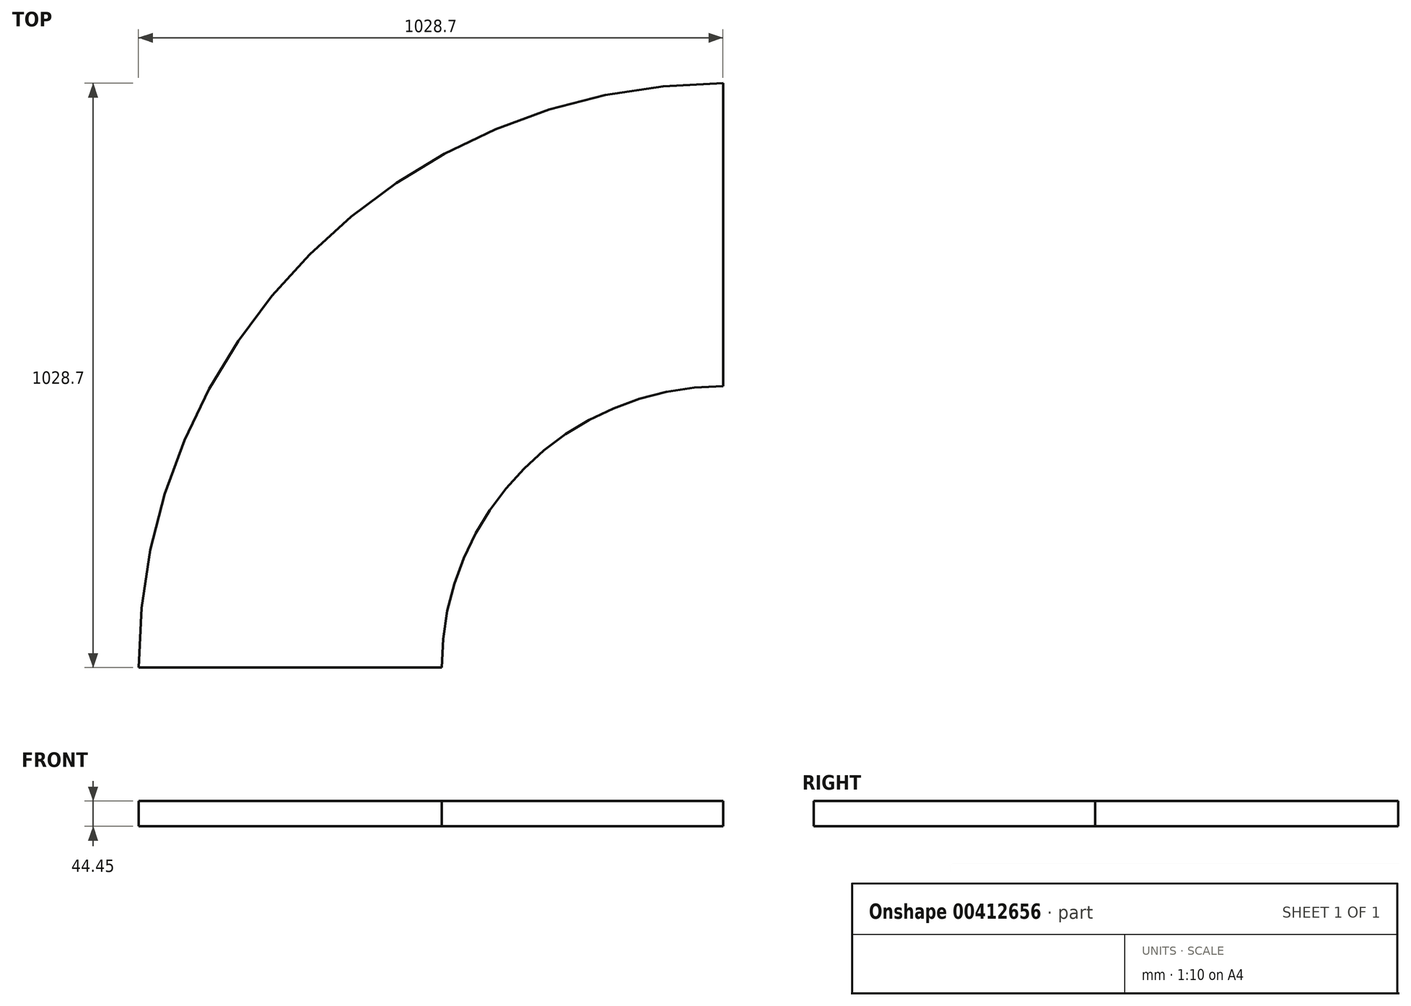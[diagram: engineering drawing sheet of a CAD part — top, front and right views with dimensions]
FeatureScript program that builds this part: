
annotation { "Feature Type Name" : "Feature", "Feature Type Description" : "" }
export const myFeature = defineFeature(function(context is Context, id is Id, definition is map)
    precondition{}
    {
        {
            var Q0;
            Q0=qCreatedBy(makeId("Top.planeOp"),FACE);
            var sketch = newSketch(context, id + "F0", { "sketchPlane" : qUnion([Q0])});
            skLineSegment(sketch, "E0", {"start": v(-19883.75, -1440.78) * mm, "end": v(-19387.66, -1440.78) * mm});
            skLineSegment(sketch, "E1", {"start": v(-22144.35, -1440.78) * mm, "end": v(-22334.85, -1440.78) * mm});
            skLineSegment(sketch, "E2", {"start": v(-24900.25, -1440.78) * mm, "end": v(-24900.25, -1186.8) * mm});
            skLineSegment(sketch, "E3", {"start": v(-24900.25, -1440.78) * mm, "end": v(-24595.45, -1440.78) * mm});
            skLineSegment(sketch, "E4", {"start": v(-19223.35, 939.75) * mm, "end": v(-19445.84, 939.75) * mm});
            skArc(sketch, "E5", {"start": v(-23624.14, 124.14) * mm, "mid": v(-23629.69, 120.5) * mm, "end": v(-23635.25, 116.9) * mm});
            skArc(sketch, "E6", {"start": v(-22416.05, -766.1) * mm, "mid": v(-22355.33, -972.57) * mm, "end": v(-22334.85, -1186.8) * mm});
            skLineSegment(sketch, "E7", {"start": v(-22334.85, -1186.8) * mm, "end": v(-22334.85, -1440.78) * mm});
            skLineSegment(sketch, "E8", {"start": v(-22334.85, -1440.78) * mm, "end": v(-22144.35, -1440.78) * mm});
            skLineSegment(sketch, "E9", {"start": v(-22144.35, -1440.78) * mm, "end": v(-22144.35, -1186.8) * mm});
            skArc(sketch, "E10", {"start": v(-22144.35, -1186.8) * mm, "mid": v(-21879.66, -459.96) * mm, "end": v(-21209.55, -73.54) * mm});
            skArc(sketch, "E11", {"start": v(-21209.55, -73.54) * mm, "mid": v(-20505.5, -177.37) * mm, "end": v(-20003.05, -681.36) * mm});
            skArc(sketch, "E12", {"start": v(-18796.55, -356.38) * mm, "mid": v(-18777.6, -346.4) * mm, "end": v(-18758.45, -336.8) * mm});
            skArc(sketch, "E13", {"start": v(-18758.45, -336.8) * mm, "mid": v(-18387.2, -228.46) * mm, "end": v(-18001.15, -251.63) * mm});
            skLineSegment(sketch, "E14", {"start": v(-18001.15, -251.63) * mm, "end": v(-18051.16, -107.3) * mm});
            skLineSegment(sketch, "E15", {"start": v(-18051.16, -107.3) * mm, "end": v(-18758.45, -107.3) * mm});
            skLineSegment(sketch, "E16", {"start": v(-18758.45, -107.3) * mm, "end": v(-19191.6, -107.3) * mm});
            skLineSegment(sketch, "E17", {"start": v(-19915.5, 31.7) * mm, "end": v(-19191.6, 31.7) * mm});
            skLineSegment(sketch, "E18", {"start": v(-19191.6, 31.7) * mm, "end": v(-19191.6, -692.2) * mm});
            skLineSegment(sketch, "E19", {"start": v(-19191.6, -692.2) * mm, "end": v(-19915.5, -692.2) * mm});
            skLineSegment(sketch, "E20", {"start": v(-19915.5, -692.2) * mm, "end": v(-19915.5, 31.7) * mm});
            skLineSegment(sketch, "E21", {"start": v(-7944.98, -1186.24) * mm, "end": v(-6763.86, -1186.24) * mm});
            skLineSegment(sketch, "E22", {"start": v(-6763.86, -1186.24) * mm, "end": v(-6763.86, 896.56) * mm});
            skLineSegment(sketch, "E23", {"start": v(-6763.86, 896.56) * mm, "end": v(-7944.98, 896.56) * mm});
            skLineSegment(sketch, "E24", {"start": v(-7944.98, 896.56) * mm, "end": v(-7944.98, 895.72) * mm});
            skLineSegment(sketch, "E25", {"start": v(-7944.98, 895.72) * mm, "end": v(-7944.98, 896.56) * mm});
            skArc(sketch, "E26", {"start": v(-7944.98, 895.72) * mm, "mid": v(-6945.35, -144.84) * mm, "end": v(-7944.98, -1185.4) * mm});
            skLineSegment(sketch, "E27", {"start": v(-7944.98, -1185.4) * mm, "end": v(-7944.98, -1186.24) * mm});
            skLineSegment(sketch, "E28", {"start": v(-7944.98, -1186.24) * mm, "end": v(-7944.98, -1185.4) * mm});
            skArc(sketch, "E29", {"start": v(-26035.55, -56.51) * mm, "mid": v(-26054.6, -56.76) * mm, "end": v(-26073.65, -57.33) * mm});
            skArc(sketch, "E30", {"start": v(-26073.65, -57.33) * mm, "mid": v(-26668.13, -253.5) * mm, "end": v(-27067.03, -735.95) * mm});
            skArc(sketch, "E31", {"start": v(-27067.03, -735.95) * mm, "mid": v(-27162.82, 105.98) * mm, "end": v(-27011.71, 939.75) * mm});
            skArc(sketch, "E32", {"start": v(-27011.71, 939.75) * mm, "mid": v(-26739.24, 262.5) * mm, "end": v(-26073.65, -37.34) * mm});
            skArc(sketch, "E33", {"start": v(-26073.65, -37.34) * mm, "mid": v(-26054.6, -37.93) * mm, "end": v(-26035.55, -38.15) * mm});
            skLineSegment(sketch, "E34", {"start": v(9209.44, 317.07) * mm, "end": v(9047.31, 575.14) * mm});
            skLineSegment(sketch, "E35", {"start": v(9047.31, 575.14) * mm, "end": v(9209.44, 317.07) * mm});
            skLineSegment(sketch, "E36", {"start": v(9209.44, 317.07) * mm, "end": v(9274.99, 358.25) * mm});
            skLineSegment(sketch, "E37", {"start": v(9274.99, 358.25) * mm, "end": v(9274.99, 1214.98) * mm});
            skLineSegment(sketch, "E38", {"start": v(9274.99, 1214.98) * mm, "end": v(7335.84, 1214.98) * mm});
            skLineSegment(sketch, "E39", {"start": v(7335.84, 1214.98) * mm, "end": v(7211.7, 630.91) * mm});
            skLineSegment(sketch, "E40", {"start": v(7211.7, 630.91) * mm, "end": v(6857.64, 706.17) * mm});
            skLineSegment(sketch, "E41", {"start": v(6857.64, 706.17) * mm, "end": v(6563.71, -676.62) * mm});
            skLineSegment(sketch, "E42", {"start": v(6563.71, -676.62) * mm, "end": v(7358.75, -845.61) * mm});
            skLineSegment(sketch, "E43", {"start": v(7358.75, -845.61) * mm, "end": v(7424.3, -804.44) * mm});
            skLineSegment(sketch, "E44", {"start": v(7424.3, -804.44) * mm, "end": v(7262.17, -546.36) * mm});
            skArc(sketch, "E45", {"start": v(7262.17, -546.36) * mm, "mid": v(7100.9, 38.05) * mm, "end": v(7288.24, 614.64) * mm});
            skArc(sketch, "E46", {"start": v(7288.24, 614.64) * mm, "mid": v(8178.4, 1068.22) * mm, "end": v(9047.31, 575.14) * mm});
            skArc(sketch, "E47", {"start": v(-26035.55, -56.51) * mm, "mid": v(-25233.08, -385.8) * mm, "end": v(-24900.25, -1186.8) * mm});
            skLineSegment(sketch, "E48", {"start": v(-24900.25, -1186.8) * mm, "end": v(-24900.25, -1440.78) * mm});
            skLineSegment(sketch, "E49", {"start": v(-24900.25, -1440.78) * mm, "end": v(-24829.05, -1440.78) * mm});
            skArc(sketch, "E50", {"start": v(-21209.55, 357.7) * mm, "mid": v(-21296.65, 498.93) * mm, "end": v(-21358.61, 652.85) * mm});
            skArc(sketch, "E51", {"start": v(-21358.61, 652.85) * mm, "mid": v(-21762.75, 118.4) * mm, "end": v(-22416.05, -30.44) * mm});
            skArc(sketch, "E52", {"start": v(-22416.05, -30.44) * mm, "mid": v(-22923.26, 191.64) * mm, "end": v(-23228.56, 653.55) * mm});
            skArc(sketch, "E53", {"start": v(-23228.56, 653.55) * mm, "mid": v(-23379.7, 355.18) * mm, "end": v(-23622.55, 125.19) * mm});
            skArc(sketch, "E54", {"start": v(-23635.25, -69.38) * mm, "mid": v(-23628.9, -68.43) * mm, "end": v(-23622.55, -67.52) * mm});
            skArc(sketch, "E55", {"start": v(-23622.55, 125.19) * mm, "mid": v(-24242.78, -34.94) * mm, "end": v(-24829.05, 223.15) * mm});
            skLineSegment(sketch, "E56", {"start": v(-30175.2, -6534.7) * mm, "end": v(-30175.2, 5657.3) * mm});
            skLineSegment(sketch, "E57", {"start": v(-30175.2, 5657.3) * mm, "end": v(30710.16, 5657.3) * mm});
            skLineSegment(sketch, "E58", {"start": v(30710.16, 5657.3) * mm, "end": v(30710.16, -6534.7) * mm});
            skLineSegment(sketch, "E59", {"start": v(30710.16, -6534.7) * mm, "end": v(-30175.2, -6534.7) * mm});
            skLineSegment(sketch, "E60", {"start": v(-30175.2, 5657.3) * mm, "end": v(-14935.2, 5657.3) * mm});
            skLineSegment(sketch, "E61", {"start": v(-14935.2, 5657.3) * mm, "end": v(-14935.2, -6534.7) * mm});
            skCircle(sketch, "E62", {"center": v(8154.74, 14.39) * mm, "radius": 533.4 * mm});
            skArc(sketch, "E63", {"start": v(8531.12, 250.85) * mm, "mid": v(7918.28, 390.77) * mm, "end": v(7778.35, -222.07) * mm});
            skArc(sketch, "E64", {"start": v(9047.31, 575.14) * mm, "mid": v(7593.99, 906.96) * mm, "end": v(7262.17, -546.36) * mm});
            skLineSegment(sketch, "E65", {"start": v(7531.84, -736.88) * mm, "end": v(7940.48, -480.15) * mm});
            skLineSegment(sketch, "E66", {"start": v(7531.84, -736.88) * mm, "end": v(7424.3, -804.44) * mm});
            skLineSegment(sketch, "E67", {"start": v(7778.35, -222.07) * mm, "end": v(7940.48, -480.15) * mm});
            skLineSegment(sketch, "E68", {"start": v(7262.17, -546.36) * mm, "end": v(7424.3, -804.44) * mm});
            skLineSegment(sketch, "E69", {"start": v(9101.9, 249.5) * mm, "end": v(8693.26, -7.22) * mm});
            skLineSegment(sketch, "E70", {"start": v(9101.9, 249.5) * mm, "end": v(9209.44, 317.07) * mm});
            skLineSegment(sketch, "E71", {"start": v(8531.12, 250.85) * mm, "end": v(8693.26, -7.22) * mm});
            skLineSegment(sketch, "E72", {"start": v(8939.77, 507.58) * mm, "end": v(9101.9, 249.5) * mm});
            skLineSegment(sketch, "E73", {"start": v(7369.7, -478.8) * mm, "end": v(7531.84, -736.88) * mm});
            skArc(sketch, "E74", {"start": v(8939.77, 507.58) * mm, "mid": v(7661.55, 799.42) * mm, "end": v(7369.7, -478.8) * mm});
            skCircle(sketch, "E75", {"center": v(-23465.15, -1186.8) * mm, "radius": 609.6 * mm});
            skLineSegment(sketch, "E76", {"start": v(-24493.85, -1491.58) * mm, "end": v(-23985.85, -1491.58) * mm});
            skLineSegment(sketch, "E77", {"start": v(-22944.45, -1491.58) * mm, "end": v(-22436.45, -1491.58) * mm});
            skLineSegment(sketch, "E78", {"start": v(-24493.85, -1491.58) * mm, "end": v(-24595.45, -1491.58) * mm});
            skLineSegment(sketch, "E79", {"start": v(-22334.85, -1491.58) * mm, "end": v(-22436.45, -1491.58) * mm});
            skLineSegment(sketch, "E80", {"start": v(-22944.45, -1491.58) * mm, "end": v(-22944.45, -1186.8) * mm});
            skArc(sketch, "E81", {"start": v(-22944.45, -1186.8) * mm, "mid": v(-23465.15, -666.1) * mm, "end": v(-23985.85, -1186.8) * mm});
            skLineSegment(sketch, "E82", {"start": v(-23985.85, -1186.8) * mm, "end": v(-23985.85, -1491.58) * mm});
            skLineSegment(sketch, "E83", {"start": v(-22461.85, -1491.58) * mm, "end": v(-22461.85, -1186.8) * mm});
            skArc(sketch, "E84", {"start": v(-22461.85, -1186.8) * mm, "mid": v(-23465.15, -183.5) * mm, "end": v(-24468.45, -1186.8) * mm});
            skLineSegment(sketch, "E85", {"start": v(-24468.45, -1186.8) * mm, "end": v(-24468.45, -1491.58) * mm});
            skLineSegment(sketch, "E86", {"start": v(-24595.45, -1491.58) * mm, "end": v(-24595.45, -1186.8) * mm});
            skArc(sketch, "E87", {"start": v(-24595.45, -1186.8) * mm, "mid": v(-23465.15, -56.5) * mm, "end": v(-22334.85, -1186.8) * mm});
            skLineSegment(sketch, "E88", {"start": v(-22334.85, -1186.8) * mm, "end": v(-22334.85, -1491.58) * mm});
            skCircle(sketch, "E89", {"center": v(-21014.05, -1186.8) * mm, "radius": 609.6 * mm});
            skLineSegment(sketch, "E90", {"start": v(-22042.75, -1491.58) * mm, "end": v(-21534.75, -1491.58) * mm});
            skLineSegment(sketch, "E91", {"start": v(-20493.35, -1491.58) * mm, "end": v(-19985.35, -1491.58) * mm});
            skLineSegment(sketch, "E92", {"start": v(-22042.75, -1491.58) * mm, "end": v(-22144.35, -1491.58) * mm});
            skLineSegment(sketch, "E93", {"start": v(-19883.75, -1491.58) * mm, "end": v(-19985.35, -1491.58) * mm});
            skLineSegment(sketch, "E94", {"start": v(-20493.35, -1491.58) * mm, "end": v(-20493.35, -1186.8) * mm});
            skArc(sketch, "E95", {"start": v(-20493.35, -1186.8) * mm, "mid": v(-21014.05, -666.1) * mm, "end": v(-21534.75, -1186.8) * mm});
            skLineSegment(sketch, "E96", {"start": v(-21534.75, -1186.8) * mm, "end": v(-21534.75, -1491.58) * mm});
            skLineSegment(sketch, "E97", {"start": v(-22144.35, -1491.58) * mm, "end": v(-22144.35, -1186.8) * mm});
            skArc(sketch, "E98", {"start": v(-22144.35, -1186.8) * mm, "mid": v(-21014.05, -56.5) * mm, "end": v(-19883.75, -1186.8) * mm});
            skLineSegment(sketch, "E99", {"start": v(-19883.75, -1186.8) * mm, "end": v(-19883.75, -1491.58) * mm});
            skCircle(sketch, "E100", {"center": v(-18260.88, -1351.68) * mm, "radius": 609.6 * mm});
            skArc(sketch, "E101", {"start": v(-17495.42, -2183.33) * mm, "mid": v(-17871.86, -290.44) * mm, "end": v(-19382.5, -1491.58) * mm});
            skArc(sketch, "E102", {"start": v(-17908.25, -1734.8) * mm, "mid": v(-18051.7, -874.85) * mm, "end": v(-18781.58, -1351.68) * mm});
            skLineSegment(sketch, "E103", {"start": v(-17495.42, -2183.33) * mm, "end": v(-17908.25, -1734.8) * mm});
            skLineSegment(sketch, "E104", {"start": v(-19883.75, -1491.58) * mm, "end": v(-19883.75, -1440.78) * mm});
            skCircle(sketch, "E105", {"center": v(-26030.55, -1186.8) * mm, "radius": 609.6 * mm});
            skLineSegment(sketch, "E106", {"start": v(-25001.85, -1491.58) * mm, "end": v(-25509.85, -1491.58) * mm});
            skLineSegment(sketch, "E107", {"start": v(-24900.25, -1491.58) * mm, "end": v(-24900.25, -1186.8) * mm});
            skArc(sketch, "E108", {"start": v(-24900.25, -1186.8) * mm, "mid": v(-26560.4, -188.39) * mm, "end": v(-26664.1, -2122.86) * mm});
            skArc(sketch, "E109", {"start": v(-25027.25, -1186.8) * mm, "mid": v(-26500.86, -300.57) * mm, "end": v(-26592.9, -2017.68) * mm});
            skLineSegment(sketch, "E110", {"start": v(-25001.85, -1491.58) * mm, "end": v(-24900.25, -1491.58) * mm});
            skArc(sketch, "E111", {"start": v(-26322.4, -1618.02) * mm, "mid": v(-26274.63, -726.86) * mm, "end": v(-25509.85, -1186.8) * mm});
            skLineSegment(sketch, "E112", {"start": v(-25509.85, -1186.8) * mm, "end": v(-25509.85, -1491.58) * mm});
            skLineSegment(sketch, "E113", {"start": v(-20010.75, -1491.58) * mm, "end": v(-20010.75, -1186.8) * mm});
            skArc(sketch, "E114", {"start": v(-20010.75, -1186.8) * mm, "mid": v(-21014.05, -183.5) * mm, "end": v(-22017.35, -1186.8) * mm});
            skLineSegment(sketch, "E115", {"start": v(-22017.35, -1186.8) * mm, "end": v(-22017.35, -1491.58) * mm});
            skArc(sketch, "E116", {"start": v(-17581.43, -2089.9) * mm, "mid": v(-17923.02, -406.98) * mm, "end": v(-19254.38, -1491.58) * mm});
            skLineSegment(sketch, "E117", {"start": v(-24976.45, -1186.8) * mm, "end": v(-24976.45, -1491.58) * mm});
            skLineSegment(sketch, "E118", {"start": v(-25027.25, -1186.8) * mm, "end": v(-25027.25, -1491.58) * mm});
            skLineSegment(sketch, "E119", {"start": v(-26664.1, -2122.86) * mm, "end": v(-26322.4, -1618.02) * mm});
            skLineSegment(sketch, "E120", {"start": v(-19382.5, -1491.58) * mm, "end": v(-18781.58, -1491.58) * mm});
            skLineSegment(sketch, "E121", {"start": v(-18781.58, -1351.68) * mm, "end": v(-18781.58, -1491.58) * mm});
            skArc(sketch, "E122", {"start": v(-23622.55, -67.52) * mm, "mid": v(-22898.77, -208.64) * mm, "end": v(-22416.05, -766.1) * mm});
            skArc(sketch, "E123", {"start": v(-20003.05, -681.36) * mm, "mid": v(-19990, -708.37) * mm, "end": v(-19977.65, -735.73) * mm});
            skArc(sketch, "E124", {"start": v(-19977.65, -735.73) * mm, "mid": v(-19907.47, -956.43) * mm, "end": v(-19883.75, -1186.8) * mm});
            skLineSegment(sketch, "E125", {"start": v(-19883.75, -1186.8) * mm, "end": v(-19883.75, -1440.78) * mm});
            skArc(sketch, "E126", {"start": v(-19387.66, -1440.78) * mm, "mid": v(-19253.31, -810.7) * mm, "end": v(-18796.55, -356.38) * mm});
            skArc(sketch, "E127", {"start": v(-20003.05, 56.97) * mm, "mid": v(-20660.26, -9.12) * mm, "end": v(-21209.55, 357.7) * mm});
            skLineSegment(sketch, "E128", {"start": v(-24519.25, -120.7) * mm, "end": v(-24519.25, -577.9) * mm});
            skLineSegment(sketch, "E129", {"start": v(-24519.25, -577.9) * mm, "end": v(-24976.45, -577.9) * mm});
            skLineSegment(sketch, "E130", {"start": v(-24976.45, -577.9) * mm, "end": v(-24976.45, -120.7) * mm});
            skLineSegment(sketch, "E131", {"start": v(-24976.45, -120.7) * mm, "end": v(-24519.25, -120.7) * mm});
            skArc(sketch, "E132", {"start": v(-24829.05, 223.15) * mm, "mid": v(-24992.32, 420.54) * mm, "end": v(-25098.73, 653.55) * mm});
            skArc(sketch, "E133", {"start": v(-25098.73, 653.55) * mm, "mid": v(-25452.96, 153.05) * mm, "end": v(-26035.55, -38.15) * mm});
            skLineSegment(sketch, "E134", {"start": v(-24829.05, -1440.78) * mm, "end": v(-24595.45, -1440.78) * mm});
            skLineSegment(sketch, "E135", {"start": v(-24595.45, -1440.78) * mm, "end": v(-24595.45, -1186.8) * mm});
            skArc(sketch, "E136", {"start": v(-24595.45, -1186.8) * mm, "mid": v(-24322.42, -450.15) * mm, "end": v(-23635.25, -69.38) * mm});
            skCircle(sketch, "E137", {"center": v(-24163.65, 939.75) * mm, "radius": 457.2 * mm});
            skArc(sketch, "E138", {"start": v(-24902.75, 518.14) * mm, "mid": v(-24167.3, 88.86) * mm, "end": v(-23428.19, 511.81) * mm});
            skArc(sketch, "E139", {"start": v(-25098.73, 653.55) * mm, "mid": v(-24163.65, -38.15) * mm, "end": v(-23228.56, 653.55) * mm});
            skArc(sketch, "E140", {"start": v(-24564.03, 911.62) * mm, "mid": v(-25102.8, 1111.21) * mm, "end": v(-25637.83, 901.84) * mm});
            skArc(sketch, "E141", {"start": v(-24517.82, 838.72) * mm, "mid": v(-24535.66, 878.5) * mm, "end": v(-24564.03, 911.62) * mm});
            skArc(sketch, "E142", {"start": v(-24517.82, 838.72) * mm, "mid": v(-24166.57, 571.46) * mm, "end": v(-23811.12, 833.1) * mm});
            skArc(sketch, "E143", {"start": v(-23767.67, 901.84) * mm, "mid": v(-23794.06, 870.42) * mm, "end": v(-23811.12, 833.1) * mm});
            skLineSegment(sketch, "E144", {"start": v(-26531.71, 939.75) * mm, "end": v(-27011.71, 939.75) * mm});
            skCircle(sketch, "E145", {"center": v(-26033.81, 939.75) * mm, "radius": 457.2 * mm});
            skArc(sketch, "E146", {"start": v(-26884.71, 939.75) * mm, "mid": v(-26251.9, 117.27) * mm, "end": v(-25294.7, 518.14) * mm});
            skArc(sketch, "E147", {"start": v(-27011.71, 939.75) * mm, "mid": v(-26178.5, -27.39) * mm, "end": v(-25098.73, 653.55) * mm});
            skArc(sketch, "E148", {"start": v(-26385.98, 831.95) * mm, "mid": v(-26033.21, 571.45) * mm, "end": v(-25681.29, 833.1) * mm});
            skArc(sketch, "E149", {"start": v(-26385.98, 831.95) * mm, "mid": v(-26441.08, 909.87) * mm, "end": v(-26531.71, 939.75) * mm});
            skArc(sketch, "E150", {"start": v(-25637.83, 901.84) * mm, "mid": v(-25664.23, 870.42) * mm, "end": v(-25681.29, 833.1) * mm});
            skArc(sketch, "E151", {"start": v(-25098.73, 653.55) * mm, "mid": v(-25230.44, 583.03) * mm, "end": v(-25325.7, 467.93) * mm});
            skLineSegment(sketch, "E152", {"start": v(-25098.73, 1110.75) * mm, "end": v(-25098.73, 653.55) * mm});
            skArc(sketch, "E153", {"start": v(-24871.76, 467.93) * mm, "mid": v(-24966.62, 583.51) * mm, "end": v(-25098.73, 653.55) * mm});
            skCircle(sketch, "E154", {"center": v(-22293.48, 939.75) * mm, "radius": 457.2 * mm});
            skArc(sketch, "E155", {"start": v(-23032.58, 518.14) * mm, "mid": v(-22297.15, 88.86) * mm, "end": v(-21558.04, 511.78) * mm});
            skArc(sketch, "E156", {"start": v(-23228.56, 653.55) * mm, "mid": v(-22294.21, -38.15) * mm, "end": v(-21358.83, 652.15) * mm});
            skArc(sketch, "E157", {"start": v(-22693.86, 911.62) * mm, "mid": v(-23232.63, 1111.21) * mm, "end": v(-23767.67, 901.84) * mm});
            skArc(sketch, "E158", {"start": v(-22647.65, 838.72) * mm, "mid": v(-22665.49, 878.5) * mm, "end": v(-22693.86, 911.62) * mm});
            skArc(sketch, "E159", {"start": v(-22647.65, 838.72) * mm, "mid": v(-22293.64, 571.45) * mm, "end": v(-21939.4, 838.4) * mm});
            skArc(sketch, "E160", {"start": v(-21892.65, 911.67) * mm, "mid": v(-21921.36, 878.44) * mm, "end": v(-21939.4, 838.4) * mm});
            skLineSegment(sketch, "E161", {"start": v(-23228.56, 1110.75) * mm, "end": v(-23228.56, 653.55) * mm});
            skArc(sketch, "E162", {"start": v(-23001.59, 467.93) * mm, "mid": v(-23096.46, 583.51) * mm, "end": v(-23228.56, 653.55) * mm});
            skArc(sketch, "E163", {"start": v(-23228.56, 653.55) * mm, "mid": v(-23360.67, 583.51) * mm, "end": v(-23455.54, 467.93) * mm});
            skLineSegment(sketch, "E164", {"start": v(-19925.85, 939.75) * mm, "end": v(-19445.84, 939.75) * mm});
            skCircle(sketch, "E165", {"center": v(-20423.74, 939.75) * mm, "radius": 457.2 * mm});
            skArc(sketch, "E166", {"start": v(-21162.85, 518.14) * mm, "mid": v(-20205.65, 117.27) * mm, "end": v(-19572.84, 939.75) * mm});
            skArc(sketch, "E167", {"start": v(-21358.83, 653.55) * mm, "mid": v(-20279.05, -27.39) * mm, "end": v(-19445.84, 939.75) * mm});
            skArc(sketch, "E168", {"start": v(-20777.83, 838.4) * mm, "mid": v(-20427.1, 571.47) * mm, "end": v(-20071.57, 831.95) * mm});
            skArc(sketch, "E169", {"start": v(-19925.85, 939.75) * mm, "mid": v(-20016.48, 909.87) * mm, "end": v(-20071.57, 831.95) * mm});
            skArc(sketch, "E170", {"start": v(-21131.85, 467.93) * mm, "mid": v(-21227.11, 583.03) * mm, "end": v(-21358.83, 653.55) * mm});
            skLineSegment(sketch, "E171", {"start": v(-21358.83, 1110.75) * mm, "end": v(-21358.83, 653.55) * mm});
            skArc(sketch, "E172", {"start": v(-21358.83, 653.55) * mm, "mid": v(-21490.54, 583.03) * mm, "end": v(-21585.8, 467.93) * mm});
            skArc(sketch, "E173", {"start": v(-20824.58, 911.67) * mm, "mid": v(-21358.61, 1110.76) * mm, "end": v(-21892.65, 911.67) * mm});
            skArc(sketch, "E174", {"start": v(-20777.83, 838.4) * mm, "mid": v(-20795.87, 878.44) * mm, "end": v(-20824.58, 911.67) * mm});
            skArc(sketch, "E175", {"start": v(-19445.84, 939.75) * mm, "mid": v(-19589.32, 429.82) * mm, "end": v(-19977.65, 69.52) * mm});
            skArc(sketch, "E176", {"start": v(-19977.65, 69.52) * mm, "mid": v(-19990.3, 63.15) * mm, "end": v(-20003.05, 56.97) * mm});
            skLineSegment(sketch, "E177", {"start": v(-19223.35, 939.75) * mm, "end": v(-19223.35, 31.7) * mm});
            skLineSegment(sketch, "E178", {"start": v(304.8, 5657.3) * mm, "end": v(304.8, -6534.7) * mm});
            skLineSegment(sketch, "E179", {"start": v(-8291.53, 769.56) * mm, "end": v(-8291.53, 286.96) * mm});
            skLineSegment(sketch, "E180", {"start": v(-8291.53, 769.56) * mm, "end": v(-8291.53, 896.56) * mm});
            skLineSegment(sketch, "E181", {"start": v(-8291.53, -1186.24) * mm, "end": v(-8291.53, -1059.24) * mm});
            skLineSegment(sketch, "E182", {"start": v(-8291.53, -1186.24) * mm, "end": v(-7986.75, -1186.24) * mm});
            skArc(sketch, "E183", {"start": v(-7986.75, -1186.24) * mm, "mid": v(-6945.35, -144.84) * mm, "end": v(-7986.75, 896.56) * mm});
            skLineSegment(sketch, "E184", {"start": v(-7986.75, 896.56) * mm, "end": v(-8291.53, 896.56) * mm});
            skCircle(sketch, "E185", {"center": v(-7986.75, -144.84) * mm, "radius": 508 * mm});
            skLineSegment(sketch, "E186", {"start": v(-8291.53, -1059.24) * mm, "end": v(-8291.53, -576.64) * mm});
            skLineSegment(sketch, "E187", {"start": v(-8291.53, -1059.24) * mm, "end": v(-7986.75, -1059.24) * mm});
            skArc(sketch, "E188", {"start": v(-7986.75, -1059.24) * mm, "mid": v(-7072.35, -144.84) * mm, "end": v(-7986.75, 769.56) * mm});
            skLineSegment(sketch, "E189", {"start": v(-7986.75, 769.56) * mm, "end": v(-8291.53, 769.56) * mm});
            skLineSegment(sketch, "E190", {"start": v(-8291.53, -576.64) * mm, "end": v(-7986.75, -576.64) * mm});
            skArc(sketch, "E191", {"start": v(-7986.75, -576.64) * mm, "mid": v(-7554.95, -144.84) * mm, "end": v(-7986.75, 286.96) * mm});
            skLineSegment(sketch, "E192", {"start": v(-7986.75, 286.96) * mm, "end": v(-8291.53, 286.96) * mm});
            skLineSegment(sketch, "E193", {"start": v(15544.8, 5657.3) * mm, "end": v(15544.8, -6534.7) * mm});
            skCircle(sketch, "E194", {"center": v(24116.36, -173.38) * mm, "radius": 660.4 * mm});
            skArc(sketch, "E195", {"start": v(24192.56, -778.2) * mm, "mid": v(24563.04, 241.46) * mm, "end": v(23518.82, -52.74) * mm});
            skArc(sketch, "E196", {"start": v(24252.89, -1257.01) * mm, "mid": v(24916.66, 569.87) * mm, "end": v(23045.76, 42.76) * mm});
            skArc(sketch, "E197", {"start": v(24268.76, -1383.02) * mm, "mid": v(25009.72, 656.3) * mm, "end": v(22921.27, 67.9) * mm});
            skLineSegment(sketch, "E198", {"start": v(22921.27, 67.9) * mm, "end": v(23518.82, -52.74) * mm});
            skLineSegment(sketch, "E199", {"start": v(24268.76, -1383.02) * mm, "end": v(24192.56, -778.2) * mm});
            skLineSegment(sketch, "E200", {"start": v(25183.16, -1525.9) * mm, "end": v(25183.16, -1856.13) * mm});
            skLineSegment(sketch, "E201", {"start": v(25183.16, -1856.13) * mm, "end": v(25487.96, -1856.13) * mm});
            skLineSegment(sketch, "E202", {"start": v(25487.96, -1856.13) * mm, "end": v(25487.96, 899.77) * mm});
            skLineSegment(sketch, "E203", {"start": v(25487.96, 899.77) * mm, "end": v(24891.06, 899.77) * mm});
            skLineSegment(sketch, "E204", {"start": v(24891.06, 899.77) * mm, "end": v(24891.06, 1325.22) * mm});
            skLineSegment(sketch, "E205", {"start": v(24891.06, 1325.22) * mm, "end": v(22617.76, 1325.22) * mm});
            skLineSegment(sketch, "E206", {"start": v(22617.76, 1325.22) * mm, "end": v(22617.76, 67.9) * mm});
            skLineSegment(sketch, "E207", {"start": v(22617.76, 67.9) * mm, "end": v(22921.27, 67.9) * mm});
            skArc(sketch, "E208", {"start": v(22921.27, 67.9) * mm, "mid": v(23671.9, 961.92) * mm, "end": v(24829.98, 815.16) * mm});
            skArc(sketch, "E209", {"start": v(24829.98, 815.16) * mm, "mid": v(25297.67, -474.98) * mm, "end": v(24268.76, -1383.02) * mm});
            skArc(sketch, "E210", {"start": v(24268.76, -1383.02) * mm, "mid": v(25297.67, -474.98) * mm, "end": v(24829.98, 815.16) * mm});
            skLineSegment(sketch, "E211", {"start": v(24268.76, -1383.02) * mm, "end": v(24268.76, -1525.9) * mm});
            skLineSegment(sketch, "E212", {"start": v(24268.76, -1525.9) * mm, "end": v(25183.16, -1525.9) * mm});
            skLineSegment(sketch, "E213", {"start": v(25183.16, -1525.9) * mm, "end": v(24268.76, -1525.9) * mm});
            skSolve(sketch);
        }
        {
            var Q0;
            Q0=qCreatedBy(makeId("Top.planeOp"),FACE);
            var sketch = newSketch(context, id + "F1", { "sketchPlane" : qUnion([Q0])});
            skLineSegment(sketch, "E214.0", {"start": v(-19191.6, -692.2) * mm, "end": v(-19915.5, -692.2) * mm});
            skArc(sketch, "E214.1", {"start": v(-22944.45, -1186.8) * mm, "mid": v(-23465.15, -666.1) * mm, "end": v(-23985.85, -1186.8) * mm});
            skLineSegment(sketch, "E214.2", {"start": v(-24519.25, -120.7) * mm, "end": v(-24519.25, -577.9) * mm});
            skArc(sketch, "E214.3", {"start": v(-19445.84, 939.75) * mm, "mid": v(-19589.32, 429.82) * mm, "end": v(-19977.65, 69.52) * mm});
            skLineSegment(sketch, "E214.4", {"start": v(-19915.5, -692.2) * mm, "end": v(-19915.5, 31.7) * mm});
            skCircle(sketch, "E214.5", {"center": v(-26033.81, 939.75) * mm, "radius": 457.2 * mm});
            skLineSegment(sketch, "E214.6", {"start": v(-24519.25, -577.9) * mm, "end": v(-24976.45, -577.9) * mm});
            skArc(sketch, "E214.7", {"start": v(-20010.75, -1186.8) * mm, "mid": v(-21014.05, -183.5) * mm, "end": v(-22017.35, -1186.8) * mm});
            skLineSegment(sketch, "E214.8", {"start": v(-23228.56, 1110.75) * mm, "end": v(-23228.56, 653.55) * mm});
            skArc(sketch, "E214.9", {"start": v(-26884.71, 939.75) * mm, "mid": v(-26251.9, 117.27) * mm, "end": v(-25294.7, 518.14) * mm});
            skLineSegment(sketch, "E214.10", {"start": v(-24976.45, -577.9) * mm, "end": v(-24976.45, -120.7) * mm});
            skLineSegment(sketch, "E214.11", {"start": v(-19223.35, 939.75) * mm, "end": v(-19223.35, 31.7) * mm});
            skArc(sketch, "E214.12", {"start": v(-22461.85, -1186.8) * mm, "mid": v(-23465.15, -183.5) * mm, "end": v(-24468.45, -1186.8) * mm});
            skArc(sketch, "E214.13", {"start": v(-27011.71, 939.75) * mm, "mid": v(-26178.5, -27.39) * mm, "end": v(-25098.73, 653.55) * mm});
            skLineSegment(sketch, "E214.14", {"start": v(-24976.45, -120.7) * mm, "end": v(-24519.25, -120.7) * mm});
            skArc(sketch, "E214.15", {"start": v(-17581.43, -2089.9) * mm, "mid": v(-17923.02, -406.98) * mm, "end": v(-19254.38, -1491.58) * mm});
            skCircle(sketch, "E214.16", {"center": v(-18260.88, -1351.68) * mm, "radius": 609.6 * mm});
            skArc(sketch, "E214.17", {"start": v(-17495.42, -2183.33) * mm, "mid": v(-17871.86, -290.44) * mm, "end": v(-19382.5, -1491.58) * mm});
            skArc(sketch, "E214.18", {"start": v(-26385.98, 831.95) * mm, "mid": v(-26033.21, 571.45) * mm, "end": v(-25681.29, 833.1) * mm});
            skArc(sketch, "E214.19", {"start": v(-17908.25, -1734.8) * mm, "mid": v(-18051.7, -874.85) * mm, "end": v(-18781.58, -1351.68) * mm});
            skCircle(sketch, "E214.20", {"center": v(-20423.74, 939.75) * mm, "radius": 457.2 * mm});
            skArc(sketch, "E214.21", {"start": v(-25098.73, 653.55) * mm, "mid": v(-25452.96, 153.05) * mm, "end": v(-26035.55, -38.15) * mm});
            skArc(sketch, "E214.22", {"start": v(-24595.45, -1186.8) * mm, "mid": v(-23465.15, -56.5) * mm, "end": v(-22334.85, -1186.8) * mm});
            skArc(sketch, "E214.23", {"start": v(-21162.85, 518.14) * mm, "mid": v(-20205.65, 117.27) * mm, "end": v(-19572.84, 939.75) * mm});
            skLineSegment(sketch, "E214.24", {"start": v(-19382.5, -1491.58) * mm, "end": v(-18781.58, -1491.58) * mm});
            skArc(sketch, "E214.25", {"start": v(-21358.83, 653.55) * mm, "mid": v(-20279.05, -27.39) * mm, "end": v(-19445.84, 939.75) * mm});
            skCircle(sketch, "E214.26", {"center": v(-26030.55, -1186.8) * mm, "radius": 609.6 * mm});
            skCircle(sketch, "E214.27", {"center": v(-21014.05, -1186.8) * mm, "radius": 609.6 * mm});
            skArc(sketch, "E214.28", {"start": v(-20777.83, 838.4) * mm, "mid": v(-20427.1, 571.47) * mm, "end": v(-20071.57, 831.95) * mm});
            skLineSegment(sketch, "E214.29", {"start": v(-25098.73, 1110.75) * mm, "end": v(-25098.73, 653.55) * mm});
            skArc(sketch, "E214.30", {"start": v(-24595.45, -1186.8) * mm, "mid": v(-24322.42, -450.15) * mm, "end": v(-23635.25, -69.38) * mm});
            skCircle(sketch, "E214.31", {"center": v(-23465.15, -1186.8) * mm, "radius": 609.6 * mm});
            skArc(sketch, "E214.32", {"start": v(-24902.75, 518.14) * mm, "mid": v(-24167.3, 88.86) * mm, "end": v(-23428.19, 511.81) * mm});
            skLineSegment(sketch, "E214.33", {"start": v(-20493.35, -1491.58) * mm, "end": v(-19985.35, -1491.58) * mm});
            skCircle(sketch, "E214.34", {"center": v(-22293.48, 939.75) * mm, "radius": 457.2 * mm});
            skArc(sketch, "E214.35", {"start": v(-23622.55, -67.52) * mm, "mid": v(-22898.77, -208.64) * mm, "end": v(-22416.05, -766.1) * mm});
            skLineSegment(sketch, "E214.36", {"start": v(-25001.85, -1491.58) * mm, "end": v(-25509.85, -1491.58) * mm});
            skLineSegment(sketch, "E214.37", {"start": v(-22042.75, -1491.58) * mm, "end": v(-21534.75, -1491.58) * mm});
            skCircle(sketch, "E214.38", {"center": v(-24163.65, 939.75) * mm, "radius": 457.2 * mm});
            skLineSegment(sketch, "E214.39", {"start": v(-24493.85, -1491.58) * mm, "end": v(-23985.85, -1491.58) * mm});
            skArc(sketch, "E214.40", {"start": v(-25098.73, 653.55) * mm, "mid": v(-24163.65, -38.15) * mm, "end": v(-23228.56, 653.55) * mm});
            skArc(sketch, "E214.41", {"start": v(-24900.25, -1186.8) * mm, "mid": v(-26560.4, -188.39) * mm, "end": v(-26664.1, -2122.86) * mm});
            skLineSegment(sketch, "E214.42", {"start": v(-21358.83, 1110.75) * mm, "end": v(-21358.83, 653.55) * mm});
            skArc(sketch, "E214.43", {"start": v(-23032.58, 518.14) * mm, "mid": v(-22297.15, 88.86) * mm, "end": v(-21558.04, 511.78) * mm});
            skLineSegment(sketch, "E214.44", {"start": v(-22944.45, -1491.58) * mm, "end": v(-22436.45, -1491.58) * mm});
            skArc(sketch, "E214.45", {"start": v(-26073.65, -57.33) * mm, "mid": v(-26668.13, -253.5) * mm, "end": v(-27067.03, -735.95) * mm});
            skArc(sketch, "E214.46", {"start": v(-24564.03, 911.62) * mm, "mid": v(-25102.8, 1111.21) * mm, "end": v(-25637.83, 901.84) * mm});
            skArc(sketch, "E214.47", {"start": v(-25027.25, -1186.8) * mm, "mid": v(-26500.86, -300.57) * mm, "end": v(-26592.9, -2017.68) * mm});
            skArc(sketch, "E214.48", {"start": v(-23228.56, 653.55) * mm, "mid": v(-22294.21, -38.15) * mm, "end": v(-21358.83, 652.15) * mm});
            skArc(sketch, "E214.49", {"start": v(-18758.45, -336.8) * mm, "mid": v(-18387.2, -228.46) * mm, "end": v(-18001.15, -251.63) * mm});
            skLineSegment(sketch, "E214.50", {"start": v(-18051.16, -107.3) * mm, "end": v(-18758.45, -107.3) * mm});
            skArc(sketch, "E214.51", {"start": v(-22144.35, -1186.8) * mm, "mid": v(-21879.66, -459.96) * mm, "end": v(-21209.55, -73.54) * mm});
            skArc(sketch, "E214.52", {"start": v(-21209.55, -73.54) * mm, "mid": v(-20505.5, -177.37) * mm, "end": v(-20003.05, -681.36) * mm});
            skLineSegment(sketch, "E214.53", {"start": v(-19883.75, -1440.78) * mm, "end": v(-19387.66, -1440.78) * mm});
            skArc(sketch, "E214.54", {"start": v(-20824.58, 911.67) * mm, "mid": v(-21358.61, 1110.76) * mm, "end": v(-21892.65, 911.67) * mm});
            skArc(sketch, "E214.55", {"start": v(-22693.86, 911.62) * mm, "mid": v(-23232.63, 1111.21) * mm, "end": v(-23767.67, 901.84) * mm});
            skArc(sketch, "E214.56", {"start": v(-26035.55, -56.51) * mm, "mid": v(-25233.08, -385.8) * mm, "end": v(-24900.25, -1186.8) * mm});
            skArc(sketch, "E214.57", {"start": v(-27067.03, -735.95) * mm, "mid": v(-27162.82, 105.98) * mm, "end": v(-27011.71, 939.75) * mm});
            skLineSegment(sketch, "E214.58", {"start": v(-19915.5, 31.7) * mm, "end": v(-19191.6, 31.7) * mm});
            skArc(sketch, "E214.59", {"start": v(-27011.71, 939.75) * mm, "mid": v(-26739.24, 262.5) * mm, "end": v(-26073.65, -37.34) * mm});
            skArc(sketch, "E214.60", {"start": v(-24517.82, 838.72) * mm, "mid": v(-24166.57, 571.46) * mm, "end": v(-23811.12, 833.1) * mm});
            skArc(sketch, "E214.61", {"start": v(-19387.66, -1440.78) * mm, "mid": v(-19253.31, -810.7) * mm, "end": v(-18796.55, -356.38) * mm});
            skArc(sketch, "E214.62", {"start": v(-26322.4, -1618.02) * mm, "mid": v(-26274.63, -726.86) * mm, "end": v(-25509.85, -1186.8) * mm});
            skArc(sketch, "E214.63", {"start": v(-20493.35, -1186.8) * mm, "mid": v(-21014.05, -666.1) * mm, "end": v(-21534.75, -1186.8) * mm});
            skLineSegment(sketch, "E214.64", {"start": v(-19191.6, 31.7) * mm, "end": v(-19191.6, -692.2) * mm});
            skArc(sketch, "E214.65", {"start": v(-20003.05, 56.97) * mm, "mid": v(-20660.26, -9.12) * mm, "end": v(-21209.55, 357.7) * mm});
            skArc(sketch, "E214.66", {"start": v(-22647.65, 838.72) * mm, "mid": v(-22293.64, 571.45) * mm, "end": v(-21939.4, 838.4) * mm});
            skLineSegment(sketch, "E214.67", {"start": v(-26531.71, 939.75) * mm, "end": v(-27011.71, 939.75) * mm});
            skArc(sketch, "E214.68", {"start": v(-21358.61, 652.85) * mm, "mid": v(-21762.75, 118.4) * mm, "end": v(-22416.05, -30.44) * mm});
            skArc(sketch, "E214.69", {"start": v(-22144.35, -1186.8) * mm, "mid": v(-21014.05, -56.5) * mm, "end": v(-19883.75, -1186.8) * mm});
            skArc(sketch, "E214.70", {"start": v(-22416.05, -30.44) * mm, "mid": v(-22923.26, 191.64) * mm, "end": v(-23228.56, 653.55) * mm});
            skLineSegment(sketch, "E214.71", {"start": v(-19925.85, 939.75) * mm, "end": v(-19445.84, 939.75) * mm});
            skArc(sketch, "E214.72", {"start": v(-23622.55, 125.19) * mm, "mid": v(-24242.78, -34.94) * mm, "end": v(-24829.05, 223.15) * mm});
            skLineSegment(sketch, "E214.73", {"start": v(-26664.1, -2122.86) * mm, "end": v(-26322.4, -1618.02) * mm});
            skLineSegment(sketch, "E214.74", {"start": v(-17495.42, -2183.33) * mm, "end": v(-17908.25, -1734.8) * mm});
            skArc(sketch, "E214.75", {"start": v(-25098.73, 653.55) * mm, "mid": v(-25230.44, 583.03) * mm, "end": v(-25325.7, 467.93) * mm});
            skLineSegment(sketch, "E214.76", {"start": v(-19883.75, -1440.78) * mm, "end": v(-19387.66, -1440.78) * mm});
            skArc(sketch, "E214.77", {"start": v(-21209.55, 357.7) * mm, "mid": v(-21296.65, 498.93) * mm, "end": v(-21358.61, 652.85) * mm});
            skArc(sketch, "E214.78", {"start": v(-21892.65, 911.67) * mm, "mid": v(-21921.36, 878.44) * mm, "end": v(-21939.4, 838.4) * mm});
            skLineSegment(sketch, "E214.79", {"start": v(-23985.85, -1186.8) * mm, "end": v(-23985.85, -1491.58) * mm});
            skArc(sketch, "E214.80", {"start": v(-19977.65, 69.52) * mm, "mid": v(-19990.3, 63.15) * mm, "end": v(-20003.05, 56.97) * mm});
            skArc(sketch, "E214.81", {"start": v(-23001.59, 467.93) * mm, "mid": v(-23096.46, 583.51) * mm, "end": v(-23228.56, 653.55) * mm});
            skArc(sketch, "E214.82", {"start": v(-23228.56, 653.55) * mm, "mid": v(-23379.7, 355.18) * mm, "end": v(-23622.55, 125.19) * mm});
            skArc(sketch, "E214.83", {"start": v(-23228.56, 653.55) * mm, "mid": v(-23360.67, 583.51) * mm, "end": v(-23455.54, 467.93) * mm});
            skArc(sketch, "E214.84", {"start": v(-24829.05, 223.15) * mm, "mid": v(-24992.32, 420.54) * mm, "end": v(-25098.73, 653.55) * mm});
            skArc(sketch, "E214.85", {"start": v(-26385.98, 831.95) * mm, "mid": v(-26441.08, 909.87) * mm, "end": v(-26531.71, 939.75) * mm});
            skLineSegment(sketch, "E214.86", {"start": v(-18781.58, -1351.68) * mm, "end": v(-18781.58, -1491.58) * mm});
            skArc(sketch, "E214.87", {"start": v(-20003.05, -681.36) * mm, "mid": v(-19990, -708.37) * mm, "end": v(-19977.65, -735.73) * mm});
            skArc(sketch, "E214.88", {"start": v(-21131.85, 467.93) * mm, "mid": v(-21227.11, 583.03) * mm, "end": v(-21358.83, 653.55) * mm});
            skArc(sketch, "E214.89", {"start": v(-19925.85, 939.75) * mm, "mid": v(-20016.48, 909.87) * mm, "end": v(-20071.57, 831.95) * mm});
            skArc(sketch, "E214.90", {"start": v(-24871.76, 467.93) * mm, "mid": v(-24966.62, 583.51) * mm, "end": v(-25098.73, 653.55) * mm});
            skArc(sketch, "E214.91", {"start": v(-19977.65, -735.73) * mm, "mid": v(-19907.47, -956.43) * mm, "end": v(-19883.75, -1186.8) * mm});
            skArc(sketch, "E214.92", {"start": v(-21358.83, 653.55) * mm, "mid": v(-21490.54, 583.03) * mm, "end": v(-21585.8, 467.93) * mm});
            skLineSegment(sketch, "E214.93", {"start": v(-18001.15, -251.63) * mm, "end": v(-18051.16, -107.3) * mm});
            skArc(sketch, "E214.94", {"start": v(-22416.05, -766.1) * mm, "mid": v(-22355.33, -972.57) * mm, "end": v(-22334.85, -1186.8) * mm});
            skArc(sketch, "E214.95", {"start": v(-18796.55, -356.38) * mm, "mid": v(-18777.6, -346.4) * mm, "end": v(-18758.45, -336.8) * mm});
            skArc(sketch, "E214.96", {"start": v(-24517.82, 838.72) * mm, "mid": v(-24535.66, 878.5) * mm, "end": v(-24564.03, 911.62) * mm});
            skLineSegment(sketch, "E214.97", {"start": v(-20493.35, -1491.58) * mm, "end": v(-20493.35, -1186.8) * mm});
            skLineSegment(sketch, "E214.98", {"start": v(-18758.45, -107.3) * mm, "end": v(-19191.6, -107.3) * mm});
            skArc(sketch, "E214.99", {"start": v(-22647.65, 838.72) * mm, "mid": v(-22665.49, 878.5) * mm, "end": v(-22693.86, 911.62) * mm});
            skLineSegment(sketch, "E214.100", {"start": v(-22944.45, -1491.58) * mm, "end": v(-22944.45, -1186.8) * mm});
            skArc(sketch, "E214.101", {"start": v(-26073.65, -37.34) * mm, "mid": v(-26054.6, -37.93) * mm, "end": v(-26035.55, -38.15) * mm});
            skLineSegment(sketch, "E214.102", {"start": v(-25509.85, -1186.8) * mm, "end": v(-25509.85, -1491.58) * mm});
            skLineSegment(sketch, "E214.103", {"start": v(-21534.75, -1186.8) * mm, "end": v(-21534.75, -1491.58) * mm});
            skArc(sketch, "E214.104", {"start": v(-26035.55, -56.51) * mm, "mid": v(-26054.6, -56.76) * mm, "end": v(-26073.65, -57.33) * mm});
            skLineSegment(sketch, "E214.105", {"start": v(-19223.35, 939.75) * mm, "end": v(-19445.84, 939.75) * mm});
            skLineSegment(sketch, "E214.106", {"start": v(-20010.75, -1491.58) * mm, "end": v(-20010.75, -1186.8) * mm});
            skLineSegment(sketch, "E214.107", {"start": v(-22461.85, -1491.58) * mm, "end": v(-22461.85, -1186.8) * mm});
            skLineSegment(sketch, "E214.108", {"start": v(-22017.35, -1186.8) * mm, "end": v(-22017.35, -1491.58) * mm});
            skArc(sketch, "E214.109", {"start": v(-23635.25, -69.38) * mm, "mid": v(-23628.9, -68.43) * mm, "end": v(-23622.55, -67.52) * mm});
            skLineSegment(sketch, "E214.110", {"start": v(-24468.45, -1186.8) * mm, "end": v(-24468.45, -1491.58) * mm});
            skArc(sketch, "E214.111", {"start": v(-25637.83, 901.84) * mm, "mid": v(-25664.23, 870.42) * mm, "end": v(-25681.29, 833.1) * mm});
            skLineSegment(sketch, "E214.112", {"start": v(-24595.45, -1440.78) * mm, "end": v(-24595.45, -1186.8) * mm});
            skLineSegment(sketch, "E214.113", {"start": v(-19883.75, -1186.8) * mm, "end": v(-19883.75, -1440.78) * mm});
            skLineSegment(sketch, "E214.114", {"start": v(-19223.35, 939.75) * mm, "end": v(-19445.84, 939.75) * mm});
            skArc(sketch, "E214.115", {"start": v(-23624.14, 124.14) * mm, "mid": v(-23629.69, 120.5) * mm, "end": v(-23635.25, 116.9) * mm});
            skLineSegment(sketch, "E214.116", {"start": v(-22334.85, -1186.8) * mm, "end": v(-22334.85, -1440.78) * mm});
            skLineSegment(sketch, "E214.117", {"start": v(-22144.35, -1440.78) * mm, "end": v(-22144.35, -1186.8) * mm});
            skArc(sketch, "E214.118", {"start": v(-20777.83, 838.4) * mm, "mid": v(-20795.87, 878.44) * mm, "end": v(-20824.58, 911.67) * mm});
            skArc(sketch, "E214.119", {"start": v(-23767.67, 901.84) * mm, "mid": v(-23794.06, 870.42) * mm, "end": v(-23811.12, 833.1) * mm});
            skLineSegment(sketch, "E214.120", {"start": v(-22144.35, -1491.58) * mm, "end": v(-22144.35, -1186.8) * mm});
            skLineSegment(sketch, "E214.121", {"start": v(-19883.75, -1186.8) * mm, "end": v(-19883.75, -1491.58) * mm});
            skLineSegment(sketch, "E214.122", {"start": v(-25027.25, -1186.8) * mm, "end": v(-25027.25, -1491.58) * mm});
            skLineSegment(sketch, "E214.123", {"start": v(-24595.45, -1491.58) * mm, "end": v(-24595.45, -1186.8) * mm});
            skLineSegment(sketch, "E214.124", {"start": v(-22334.85, -1186.8) * mm, "end": v(-22334.85, -1491.58) * mm});
            skLineSegment(sketch, "E214.125", {"start": v(-22042.75, -1491.58) * mm, "end": v(-22144.35, -1491.58) * mm});
            skLineSegment(sketch, "E214.126", {"start": v(-24900.25, -1440.78) * mm, "end": v(-24595.45, -1440.78) * mm});
            skLineSegment(sketch, "E214.127", {"start": v(-22334.85, -1440.78) * mm, "end": v(-22144.35, -1440.78) * mm});
            skLineSegment(sketch, "E214.128", {"start": v(-24493.85, -1491.58) * mm, "end": v(-24595.45, -1491.58) * mm});
            skLineSegment(sketch, "E214.129", {"start": v(-22334.85, -1491.58) * mm, "end": v(-22436.45, -1491.58) * mm});
            skLineSegment(sketch, "E214.130", {"start": v(-24900.25, -1186.8) * mm, "end": v(-24900.25, -1440.78) * mm});
            skLineSegment(sketch, "E214.131", {"start": v(-24976.45, -1186.8) * mm, "end": v(-24976.45, -1491.58) * mm});
            skLineSegment(sketch, "E214.132", {"start": v(-24829.05, -1440.78) * mm, "end": v(-24595.45, -1440.78) * mm});
            skLineSegment(sketch, "E214.133", {"start": v(-22144.35, -1440.78) * mm, "end": v(-22334.85, -1440.78) * mm});
            skLineSegment(sketch, "E214.134", {"start": v(-24900.25, -1440.78) * mm, "end": v(-24900.25, -1186.8) * mm});
            skLineSegment(sketch, "E214.135", {"start": v(-19883.75, -1491.58) * mm, "end": v(-19883.75, -1440.78) * mm});
            skLineSegment(sketch, "E214.136", {"start": v(-24900.25, -1491.58) * mm, "end": v(-24900.25, -1186.8) * mm});
            skLineSegment(sketch, "E214.137", {"start": v(-19883.75, -1491.58) * mm, "end": v(-19985.35, -1491.58) * mm});
            skLineSegment(sketch, "E214.138", {"start": v(-25001.85, -1491.58) * mm, "end": v(-24900.25, -1491.58) * mm});
            skLineSegment(sketch, "E214.139", {"start": v(-24900.25, -1440.78) * mm, "end": v(-24829.05, -1440.78) * mm});
            skSolve(sketch);
        }
        {
            var Q0;
            Q0=qCreatedBy(makeId("Top.planeOp"),FACE);
            var sketch = newSketch(context, id + "F2", { "sketchPlane" : qUnion([Q0])});
            skArc(sketch, "E215.0", {"start": v(-20010.75, -1186.8) * mm, "mid": v(-21014.05, -183.5) * mm, "end": v(-22017.35, -1186.8) * mm, "construction": true});
            skArc(sketch, "E216.0", {"start": v(-21014.05, -158.1) * mm, "mid": v(-21741.45, -459.4) * mm, "end": v(-22042.75, -1186.8) * mm});
            skArc(sketch, "E217.0", {"start": v(-21014.05, -691.5) * mm, "mid": v(-21364.28, -836.57) * mm, "end": v(-21509.35, -1186.8) * mm});
            skLineSegment(sketch, "E218", {"start": v(-21014.05, -158.1) * mm, "end": v(-21014.05, -691.5) * mm});
            skLineSegment(sketch, "E219", {"start": v(-21509.35, -1186.8) * mm, "end": v(-22042.75, -1186.8) * mm});
            skPoint(sketch, "E220.orphan", {"position": v(-21014.05, -767.55) * mm});
            skSolve(sketch);
        }
        {
            var Q0;
            Q0=makeQuery(id+"F2.imprint","IMPRINT",FACE,{"disambiguationData":[TD([[makeQuery(id+"F2.imprint","IMPRINT",EDGE,{"derivedFrom":sQuery(id+"F2.wireOp",EDGE,"E216.0")}),1.0]])]});
            extrude(context, id + "F3", {"entities" : qUnion([Q0]), "depth" : 44.45 * mm});
        }
    });
